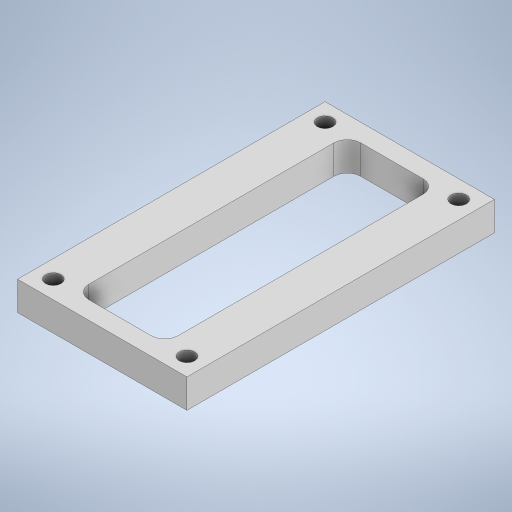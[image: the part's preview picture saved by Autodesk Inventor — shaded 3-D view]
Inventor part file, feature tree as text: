
AUTODESK INVENTOR PART (.ipt)
format: ipt  version: 2024 (Build 280153000, 153)  size: 252,928 bytes
history: native  units: mm
features: extrude x2, sketch x2
ambient origin geometry x8: Origin, YZ Plane, XZ Plane, XY Plane, X Axis, Y Axis, Z Axis, Center Point
bodies: Solid1 (feature_tree)
feature tree (4):
  extrude  "Extrusion1"  Depth=69.0mm
  extrude  "Extrusion2"  Depth=9.0mm
  sketch  "Sketch1"  dims[d0=38.0mm d1=69.0mm]
  sketch  "Sketch2"  dims[d2=4.0mm d3=9.0mm d4=4.0mm d5=9.0mm d6=3.0mm d7=6.5mm d8=0.0mm d9=3.5mm d10=4.0mm d11=4.0mm d12=4.0mm d13=4.0mm d14=6.5mm d15=0.0mm]
